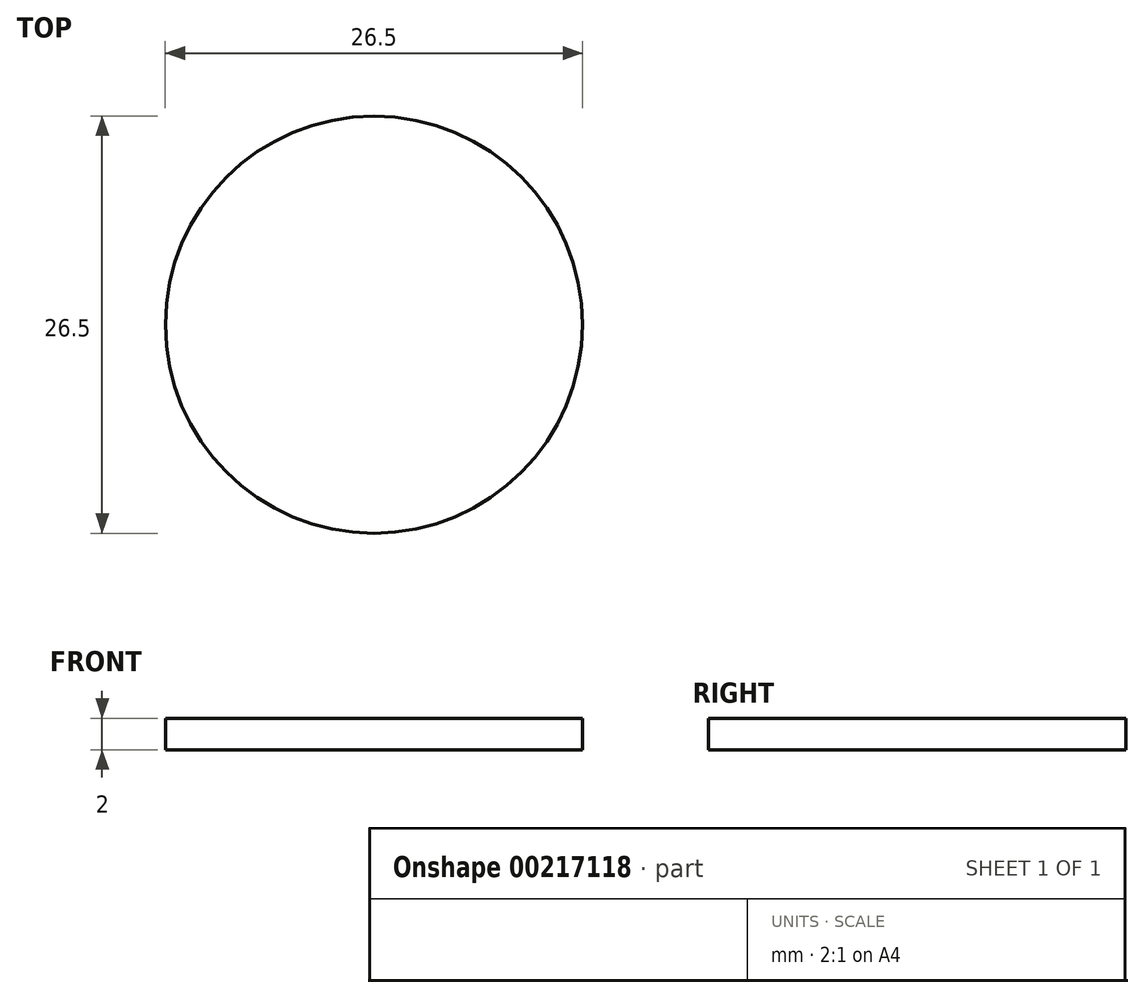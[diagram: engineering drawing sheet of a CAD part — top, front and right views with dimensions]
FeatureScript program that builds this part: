
annotation { "Feature Type Name" : "Feature", "Feature Type Description" : "" }
export const myFeature = defineFeature(function(context is Context, id is Id, definition is map)
    precondition{}
    {
        {
            var Q0;
            Q0=qCreatedBy(makeId("Top.planeOp"),FACE);
            var sketch = newSketch(context, id + "F0", { "sketchPlane" : qUnion([Q0])});
            skCircle(sketch, "E0", {"center": v(0, 0) * mm, "radius": 13.25 * mm});
            skSolve(sketch);
        }
        {
            var Q0;
            Q0 = qSketchRegion(id + "F0", true);
            extrude(context, id + "F1", {"entities" : qUnion([Q0]), "endBound" : BoundingType.SYMMETRIC, "depth" : 2 * mm});
        }
    });
